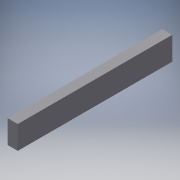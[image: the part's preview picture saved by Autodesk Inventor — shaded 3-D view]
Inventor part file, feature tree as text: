
AUTODESK INVENTOR PART (.ipt)
format: ipt  version: 2016 (Build 200138000, 138)  size: 87,040 bytes
history: native  units: in
note: dims shown in document units (in); Inventor stores cm internally (conversion verified against a paired STEP export)
features: extrude x1, sketch x1
ambient origin geometry x8: Origin, YZ Plane, XZ Plane, XY Plane, X Axis, Y Axis, Z Axis, Center Point
bodies: Solid1 (feature_tree)
feature tree (2):
  extrude  "Extrusion1"  Depth=3.5in
  sketch  "Sketch1"  dims[d0=1.5in d1=3.5in d2=23.26in d3=0.0in]
